# Revit family: Kabelrinne_630_FT_FS_FSK_FTSO_A2_A4
name_source: partatom
category: Generic Models
revit_build: Autodesk Revit 2017 (Build: 20160225_1515(x64)
units: mm (PartAtom-declared; Revit-internal decimal feet)

## family parameters
Always vertical = Yes
Can host rebar = No
Cut with Voids When Loaded = No
Part Type = Normal
Room Calculation Point = No
Round Connector Dimension = Use Diameter
Shared = No
Work Plane-Based = No

## types (6) — shared parameters
Cut's number = 2
Cut's number 2 = 60
Cut's number 3 = 59
Cut's space = 50 mm  [stored 0.164042 ft]
Height = 51 mm
Length = 3000 mm  [stored 9.84252 ft]
Manufacturer = OBO BETTERMANN
URL = http:/www.obo-bettermann.com
Width = 300 mm
Width 1 = 150 mm  [stored 0.492126 ft]

## per-type parameters (varying)
| type | Article Type | GTIN | Manufacturer Art.No. | Material |
| SKS 630 FT | SKS 630 FS | 4012196060313 | 6056296 | Strip-galvanised |
| SKS 630 FS | SKS 630 FS | 4012196060313 | 6056296 | Strip-galvanised |
| SKS 630 FSK TGN | SKS 630 FT SO | 4012196545476 | 7190131 | Strip-galvanised |
| SKS 630 FT SO | SKS 630 A2 | 4012196120673 | 6056739 | Edelstahl, rostfrei A2 |
| SKS 630 A2 | SKS 630 A4 | 4012196050161 | 6056757 | Edelstahl, rostfrei A2 |
| SKS 630 A4 | SKS 630 A4 | 4012196050161 | 6056757 | Edelstahl, rostfrei A4 |

note: [stored X ft] marks values corroborated as IEEE doubles in the binary element streams (Revit-internal decimal feet)

## geometry (parser evidence)
native form markers: Sweep x2
no freeform markers — native parametric forms only
